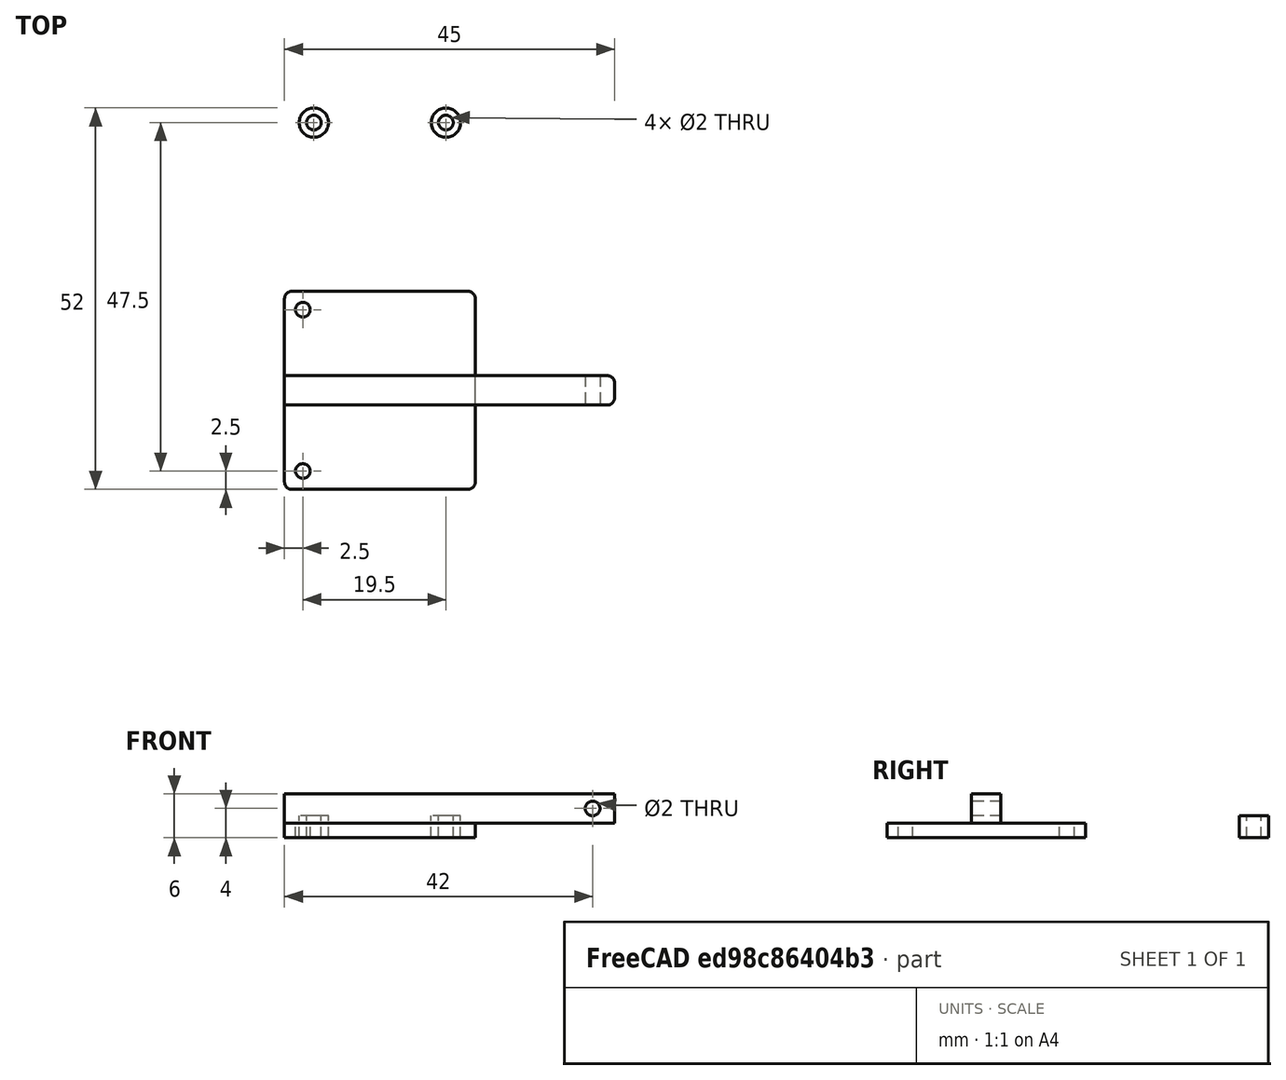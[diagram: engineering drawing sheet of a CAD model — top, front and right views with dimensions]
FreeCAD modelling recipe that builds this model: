
FCSTD DOCUMENT  (FreeCAD 0.17R13541 (Git))
Label: cam mt
License: All rights reserved
LicenseURL: http://en.wikipedia.org/wiki/All_rights_reserved
objects: Part::Cylinder×7, Part::Cut×5, Part::Box×2, Part::Fillet×2
note: 16 computed .brp shape members not serialized (recipe doc carries the construction recipe); baked Part::Feature solids carry a one-line shape summary decoded from their .brp

FEATURE [Part::Cylinder] Cylinder
  Angle = 360
  AttacherType = Attacher::AttachEngine3D
  Height = 2
  Placement = pos=(2.5,2.5,0) rot=(0,0,1;0rad)
  Radius = 1
FEATURE [Part::Box] Box  label="Cube"
  AttacherType = Attacher::AttachEngine3D
  Height = 2
  Length = 26
  Width = 27
FEATURE [Part::Cylinder] Cylinder001
  Angle = 360
  AttacherType = Attacher::AttachEngine3D
  Height = 2
  Placement = pos=(2.5,24.5,0) rot=(0,0,1;0rad)
  Radius = 1
FEATURE [Part::Cut] Cut
  Base = -> Box
  Tool = -> Cylinder
FEATURE [Part::Cut] Cut001
  Base = -> Cut
  Tool = -> Cylinder001
FEATURE [Part::Cylinder] Cylinder002
  Angle = 360
  AttacherType = Attacher::AttachEngine3D
  Height = 3
  Placement = pos=(4,50,0) rot=(0,0,1;0rad)
  Radius = 2
FEATURE [Part::Cylinder] Cylinder003
  Angle = 360
  AttacherType = Attacher::AttachEngine3D
  Height = 3
  Placement = pos=(4,50,0) rot=(0,0,1;0rad)
  Radius = 1
FEATURE [Part::Cut] Cut002
  Base = -> Cylinder002
  Tool = -> Cylinder003
FEATURE [Part::Cylinder] Cylinder004
  Angle = 360
  AttacherType = Attacher::AttachEngine3D
  Height = 3
  Placement = pos=(4,50,0) rot=(0,0,1;0rad)
  Radius = 1
FEATURE [Part::Cylinder] Cylinder005
  Angle = 360
  AttacherType = Attacher::AttachEngine3D
  Height = 3
  Placement = pos=(4,50,0) rot=(0,0,1;0rad)
  Radius = 2
FEATURE [Part::Cut] Cut003
  Base = -> Cylinder005
  Placement = pos=(18,0,0) rot=(0,0,1;0rad)
  Tool = -> Cylinder004
FEATURE [Part::Box] Box001  label="Cube001"
  AttacherType = Attacher::AttachEngine3D
  Height = 4
  Length = 45
  Placement = pos=(0,11.5,2) rot=(0,0,1;0rad)
  Width = 4
FEATURE [Part::Fillet] Fillet001
  Base = -> Cut001
  Edges = 4 edges r=1: [Edge1,Edge3,Edge6,Edge13]
FEATURE [Part::Fillet] Fillet
  Base = -> Box001
  Edges = 2 edges r=1: [Edge5,Edge7]
FEATURE [Part::Cylinder] Cylinder006
  Angle = 360
  AttacherType = Attacher::AttachEngine3D
  Height = 4
  Placement = pos=(42,15.5,4) rot=(1,0,0;1.5708rad)
  Radius = 1
  expr: Placement.Rotation.Axis.z = 0
FEATURE [Part::Cut] Cut004
  Base = -> Fillet
  Tool = -> Cylinder006
